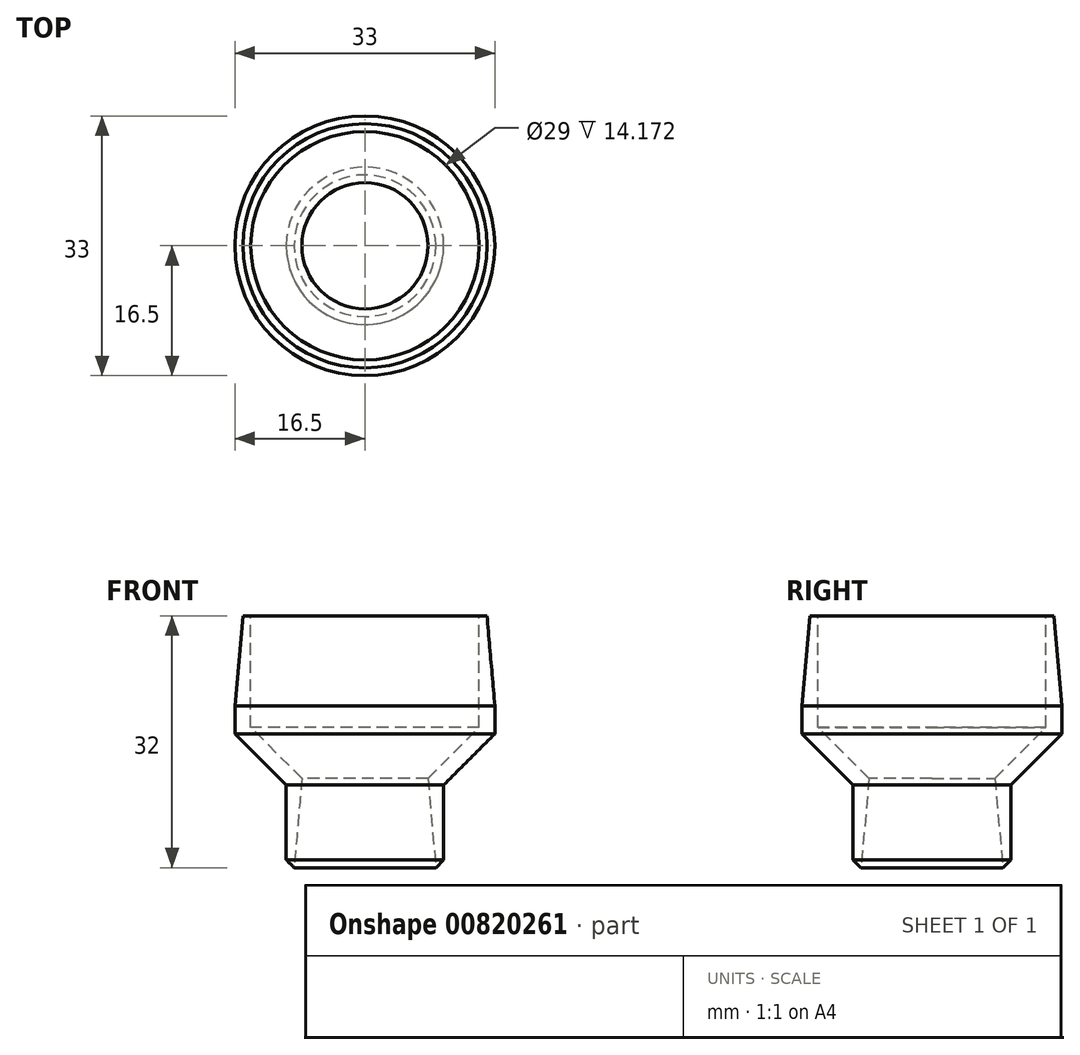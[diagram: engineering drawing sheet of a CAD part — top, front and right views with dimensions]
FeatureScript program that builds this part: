
annotation { "Feature Type Name" : "Feature", "Feature Type Description" : "" }
export const myFeature = defineFeature(function(context is Context, id is Id, definition is map)
    precondition{}
    {
        {
            var Q0;
            Q0=qCreatedBy(makeId("Front.planeOp"),FACE);
            var sketch = newSketch(context, id + "F0", { "sketchPlane" : qUnion([Q0])});
            skLineSegment(sketch, "E0", {"start": v(0, 14.67) * mm, "end": v(0, -14.37) * mm, "construction": true});
            skLineSegment(sketch, "E1", {"start": v(-16.5, 15) * mm, "end": v(-16.5, 0) * mm});
            skLineSegment(sketch, "E2", {"start": v(-16.5, 0) * mm, "end": v(-10, -6.5) * mm});
            skLineSegment(sketch, "E3", {"start": v(-10, -17) * mm, "end": v(-8, -17) * mm});
            skLineSegment(sketch, "E4", {"start": v(-8, -17) * mm, "end": v(-8, -5.67) * mm});
            skLineSegment(sketch, "E5", {"start": v(-8, -5.67) * mm, "end": v(-14.5, 0.83) * mm});
            skLineSegment(sketch, "E6", {"start": v(-14.5, 0.83) * mm, "end": v(-14.5, 15) * mm});
            skLineSegment(sketch, "E7", {"start": v(-14.5, 15) * mm, "end": v(-16.5, 15) * mm});
            skLineSegment(sketch, "E8", {"start": v(-10, -17) * mm, "end": v(-10, -6.5) * mm});
            skPoint(sketch, "E9.start.orphan", {"position": v(-14.5, -2) * mm});
            skPoint(sketch, "E10.orphan", {"position": v(-12, -17) * mm});
            skSolve(sketch);
        }
        {
            var Q0;
            Q0=makeQuery(id+"F0.imprint","IMPRINT",FACE,{"disambiguationData":[TD([[makeQuery(id+"F0.imprint","IMPRINT",EDGE,{"derivedFrom":sQuery(id+"F0.wireOp",EDGE,"E1")}),1.0]])]});
            var Q1;
            Q1=sQuery(id+"F0.wireOp",EDGE,"E0");
            revolve(context, id + "F1", {"surfaceOperationType" : NewSurfaceOperationType.NEW, "entities" : qUnion([Q0]), "axis" : qUnion([Q1]), "revolveType" : RevolveType.FULL});
        }
        {
            var Q0;
            Q0=makeQuery(id+"F1.opRevolve","SWEPT_EDGE",EDGE,{"disambiguationData":[OSD([sQuery(id+"F0.wireOp",EDGE,"E1"),sQuery(id+"F0.wireOp",EDGE,"E7")])]});
            chamfer(context, id + "F2", {"entities" : qUnion([Q0]), "chamferType" : ChamferType.OFFSET_ANGLE, "width" : 1 * mm, "oppositeDirection" : false, "angle" : 85 * degree, "tangentPropagation" : true});
        }
        {
            var Q0;
            Q0=makeQuery(id+"F1.opRevolve","SWEPT_EDGE",EDGE,{"disambiguationData":[OSD([sQuery(id+"F0.wireOp",EDGE,"E3"),sQuery(id+"F0.wireOp",EDGE,"E8")])]});
            chamfer(context, id + "F3", {"entities" : qUnion([Q0]), "width" : 1 * mm, "tangentPropagation" : true});
        }
        {
            var Q0;
            Q0=makeQuery(id+"F1.opRevolve","SWEPT_EDGE",EDGE,{"disambiguationData":[OSD([sQuery(id+"F0.wireOp",EDGE,"E3"),sQuery(id+"F0.wireOp",EDGE,"E4")])]});
            chamfer(context, id + "F4", {"entities" : qUnion([Q0]), "chamferType" : ChamferType.OFFSET_ANGLE, "width" : 1 * mm, "oppositeDirection" : false, "angle" : 85 * degree, "tangentPropagation" : true});
        }
    });
